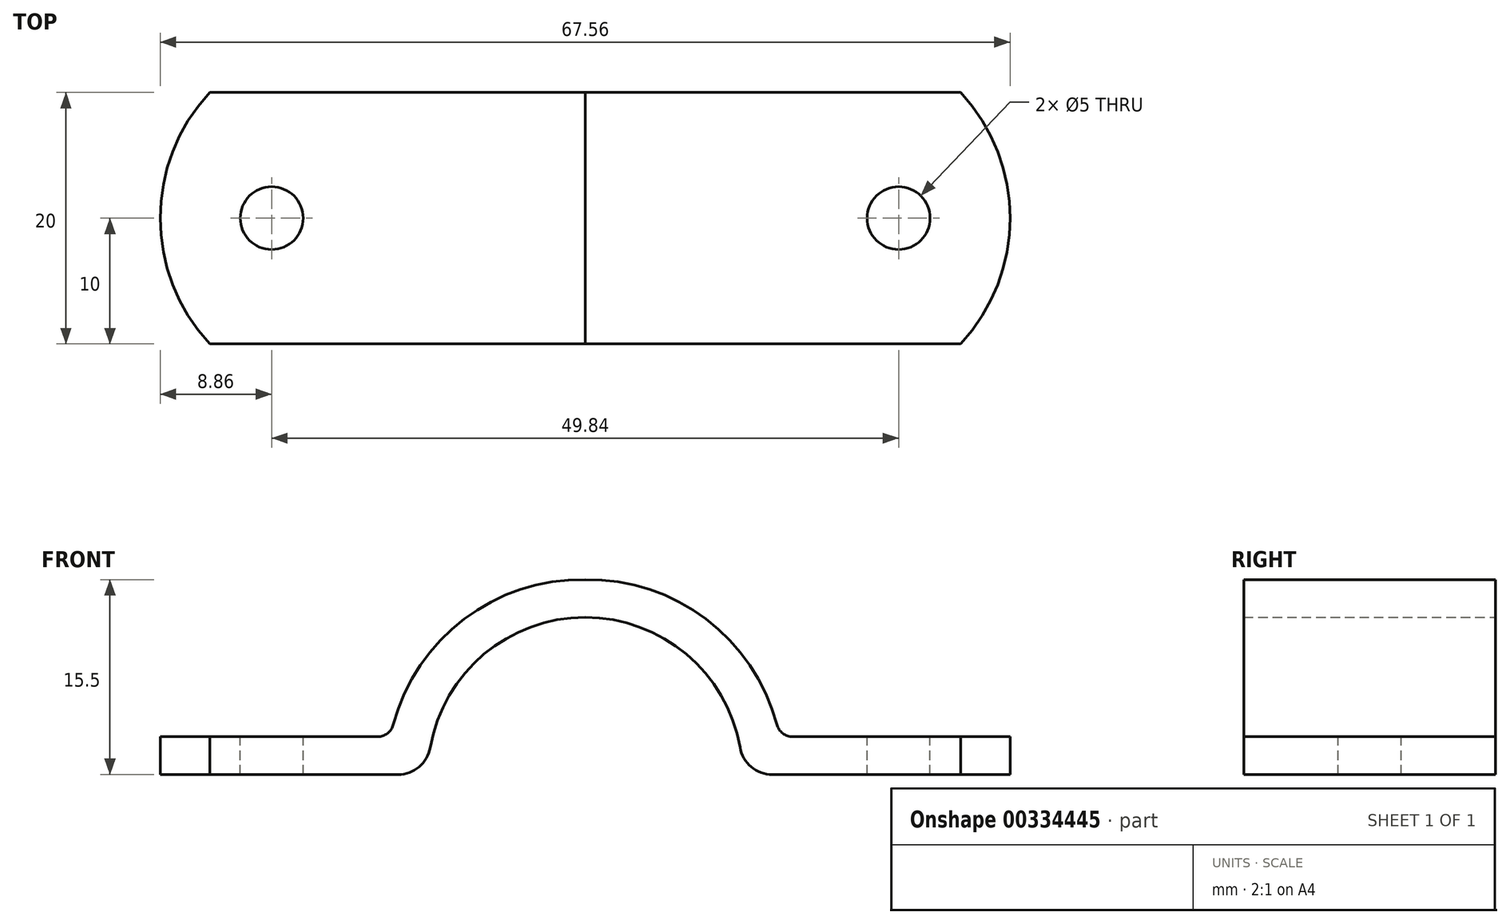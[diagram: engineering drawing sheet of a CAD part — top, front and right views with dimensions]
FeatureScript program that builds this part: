
annotation { "Feature Type Name" : "Feature", "Feature Type Description" : "" }
export const myFeature = defineFeature(function(context is Context, id is Id, definition is map)
    precondition{}
    {
        {
            var Q0;
            Q0=qCreatedBy(makeId("Front.planeOp"),FACE);
            var sketch = newSketch(context, id + "F0", { "sketchPlane" : qUnion([Q0])});
            skLineSegment(sketch, "E0", {"start": v(0, 0) * mm, "end": v(12.5, 0) * mm, "construction": true});
            skLineSegment(sketch, "E1", {"start": v(0, 0) * mm, "end": v(0, 15.5) * mm, "construction": true});
            skLineSegment(sketch, "E2", {"start": v(0, 0) * mm, "end": v(-12.5, 0) * mm, "construction": true});
            skArc(sketch, "E3", {"start": v(12.31, 2.15) * mm, "mid": v(0, 12.5) * mm, "end": v(-12.31, 2.15) * mm});
            skLineSegment(sketch, "E4", {"start": v(-14.87, 0) * mm, "end": v(-29.85, 0) * mm});
            skLineSegment(sketch, "E5", {"start": v(-29.85, 0) * mm, "end": v(-29.85, 3) * mm});
            skLineSegment(sketch, "E6", {"start": v(-29.85, 3) * mm, "end": v(-16.5, 3) * mm});
            skLineSegment(sketch, "E7", {"start": v(14.87, 0) * mm, "end": v(29.85, 0) * mm});
            skLineSegment(sketch, "E8", {"start": v(29.85, 0) * mm, "end": v(29.85, 3) * mm});
            skLineSegment(sketch, "E9", {"start": v(29.85, 3) * mm, "end": v(16.5, 3) * mm});
            skArc(sketch, "E10", {"start": v(15.25, 3.97) * mm, "mid": v(9.61, 12.36) * mm, "end": v(0, 15.5) * mm});
            skArc(sketch, "E11", {"start": v(0, 15.5) * mm, "mid": v(-9.61, 12.36) * mm, "end": v(-15.25, 3.97) * mm});
            skPoint(sketch, "E12.visualSharp", {"position": v(-15.47, 3) * mm});
            skArc(sketch, "E12.filletArc", {"start": v(-16.5, 3) * mm, "mid": v(-15.71, 3.27) * mm, "end": v(-15.25, 3.97) * mm});
            skPoint(sketch, "E13.visualSharp", {"position": v(15.47, 3) * mm});
            skArc(sketch, "E13.filletArc", {"start": v(15.25, 3.97) * mm, "mid": v(15.71, 3.27) * mm, "end": v(16.5, 3) * mm});
            skPoint(sketch, "E14.visualSharp", {"position": v(-12.5, 0) * mm});
            skArc(sketch, "E14.filletArc", {"start": v(-14.87, 0) * mm, "mid": v(-13.2, 0.6) * mm, "end": v(-12.31, 2.15) * mm});
            skPoint(sketch, "E15.visualSharp", {"position": v(12.5, 0) * mm});
            skArc(sketch, "E15.filletArc", {"start": v(12.31, 2.15) * mm, "mid": v(13.2, 0.6) * mm, "end": v(14.87, 0) * mm});
            skSolve(sketch);
        }
        {
            var Q0;
            Q0=makeQuery(id+"F0.imprint","IMPRINT",FACE,{"disambiguationData":[TD([[makeQuery(id+"F0.imprint","IMPRINT",EDGE,{"derivedFrom":sQuery(id+"F0.wireOp",EDGE,"E3")}),-1.0]])]});
            extrude(context, id + "F1", {"entities" : qUnion([Q0]), "depth" : 20 * mm, "symmetric" : true});
        }
        {
            var Q0;
            Q0=makeQuery(id+"F1.opExtrude","SWEPT_FACE",FACE,{"disambiguationData":[OSD([sQuery(id+"F0.wireOp",EDGE,"E6")])]});
            var sketch = newSketch(context, id + "F2", { "sketchPlane" : qUnion([Q0])});
            skCircle(sketch, "E16", {"center": v(-24.92, 0) * mm, "radius": 2.5 * mm});
            skCircle(sketch, "E17", {"center": v(24.92, 0) * mm, "radius": 2.5 * mm});
            skSolve(sketch);
        }
        {
            var Q0;
            Q0=makeQuery(id+"F2.imprint","IMPRINT",FACE,{"disambiguationData":[TD([[makeQuery(id+"F2.imprint","IMPRINT",EDGE,{"derivedFrom":sQuery(id+"F2.wireOp",EDGE,"E16")}),1.0]])]});
            var Q1;
            Q1=makeQuery(id+"F2.imprint","IMPRINT",FACE,{"disambiguationData":[TD([[makeQuery(id+"F2.imprint","IMPRINT",EDGE,{"derivedFrom":sQuery(id+"F2.wireOp",EDGE,"E17")}),1.0]])]});
            extrude(context, id + "F3", {"entities" : qUnion([Q0, Q1]), "operationType" : NewBodyOperationType.REMOVE, "oppositeDirection" : true, "depth" : 25 * mm});
        }
        {
            var Q0;
            Q0=makeQuery(id+"F1.opExtrude","SWEPT_FACE",FACE,{"disambiguationData":[OSD([sQuery(id+"F0.wireOp",EDGE,"E6")])]});
            var sketch = newSketch(context, id + "F4", { "sketchPlane" : qUnion([Q0])});
            skArc(sketch, "E18", {"start": v(-29.85, 10) * mm, "mid": v(-33.78, 0) * mm, "end": v(-29.85, -10) * mm});
            skSolve(sketch);
        }
        {
            var Q0;
            Q0=makeQuery(id+"F4.imprint","IMPRINT",FACE,{"disambiguationData":[TD([[makeQuery(id+"F4.imprint","IMPRINT",EDGE,{"derivedFrom":sQuery(id+"F4.wireOp",EDGE,"E18")}),1.0]])]});
            extrude(context, id + "F5", {"entities" : qUnion([Q0]), "operationType" : NewBodyOperationType.ADD, "oppositeDirection" : true, "depth" : 3 * mm});
        }
        {
            var Q0;
            Q0=makeQuery(id+"F1.opExtrude","SWEPT_FACE",FACE,{"disambiguationData":[OSD([sQuery(id+"F0.wireOp",EDGE,"E9")])]});
            var sketch = newSketch(context, id + "F6", { "sketchPlane" : qUnion([Q0])});
            skArc(sketch, "E19", {"start": v(29.85, -10) * mm, "mid": v(33.78, 0) * mm, "end": v(29.85, 10) * mm});
            skSolve(sketch);
        }
        {
            var Q0;
            Q0=makeQuery(id+"F6.imprint","IMPRINT",FACE,{"disambiguationData":[TD([[makeQuery(id+"F6.imprint","IMPRINT",EDGE,{"derivedFrom":sQuery(id+"F6.wireOp",EDGE,"E19")}),1.0]])]});
            extrude(context, id + "F7", {"entities" : qUnion([Q0]), "operationType" : NewBodyOperationType.ADD, "oppositeDirection" : true, "depth" : 3 * mm});
        }
    });
